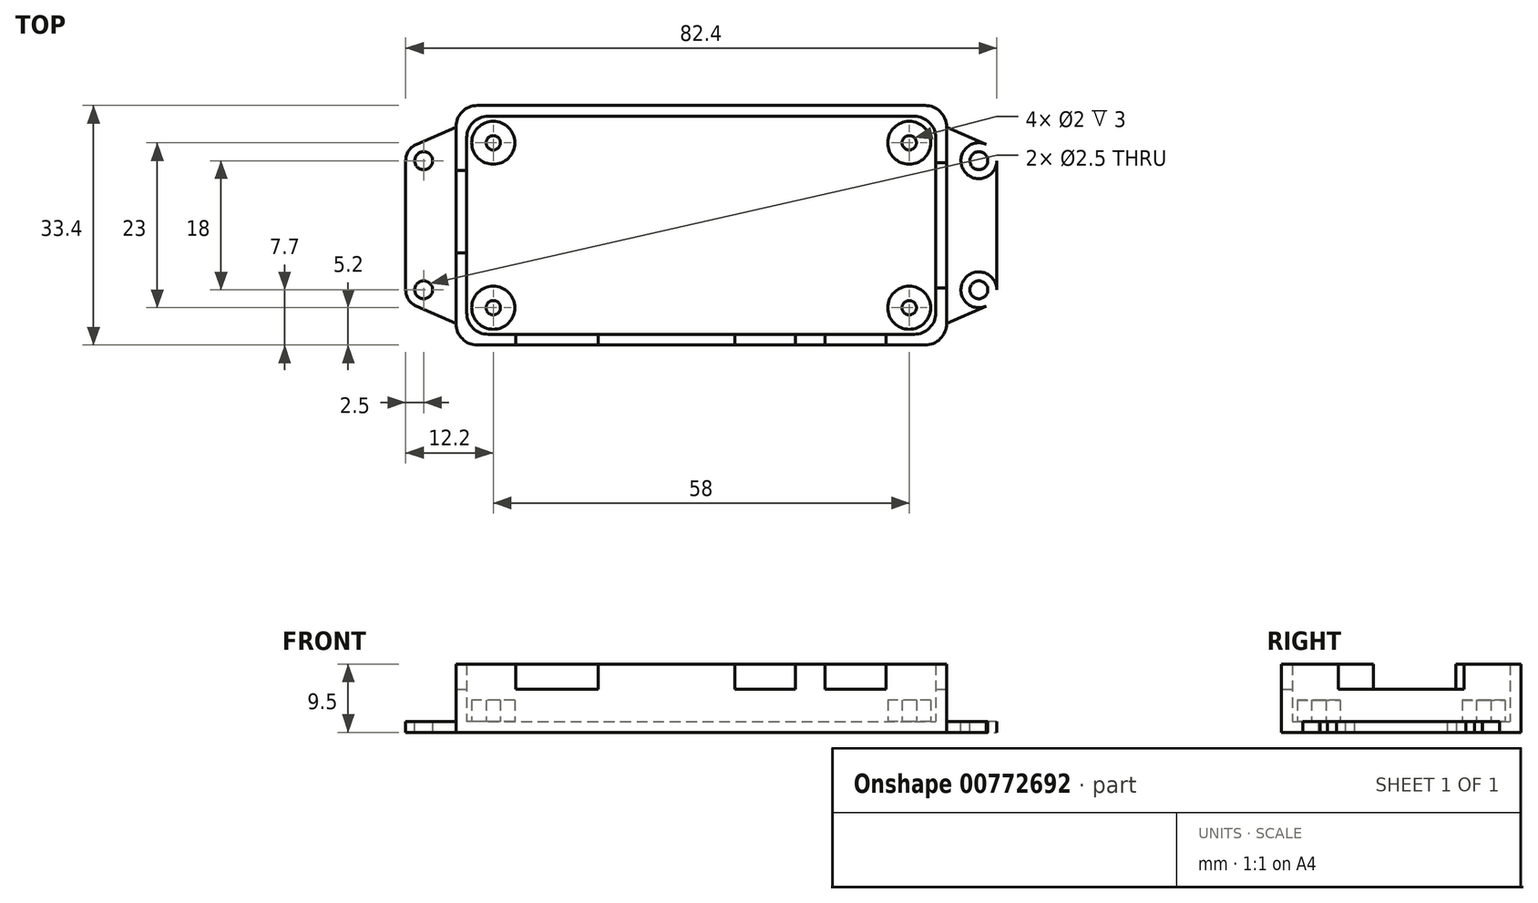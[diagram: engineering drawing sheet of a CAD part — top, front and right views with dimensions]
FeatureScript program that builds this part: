
annotation { "Feature Type Name" : "Feature", "Feature Type Description" : "" }
export const myFeature = defineFeature(function(context is Context, id is Id, definition is map)
    precondition{}
    {
        {
            var Q0;
            Q0=qCreatedBy(makeId("Top.planeOp"),FACE);
            var sketch = newSketch(context, id + "F0", { "sketchPlane" : qUnion([Q0])});
            skLineSegment(sketch, "E0", {"start": v(0, 31.79) * mm, "end": v(0, -34.92) * mm, "construction": true});
            skLineSegment(sketch, "E1", {"start": v(-57.68, 0) * mm, "end": v(57.82, 0) * mm, "construction": true});
            skLineSegment(sketch, "E2.bottom", {"start": v(-29.5, 15) * mm, "end": v(29.5, 15) * mm, "construction": true});
            skLineSegment(sketch, "E2.top", {"start": v(-29.5, -15) * mm, "end": v(29.5, -15) * mm, "construction": true});
            skLineSegment(sketch, "E2.left", {"start": v(-32.5, 12) * mm, "end": v(-32.5, -12) * mm, "construction": true});
            skLineSegment(sketch, "E2.right", {"start": v(32.5, 12) * mm, "end": v(32.5, -12) * mm, "construction": true});
            skPoint(sketch, "E3.visualSharp", {"position": v(-32.5, 15) * mm});
            skArc(sketch, "E3.filletArc", {"start": v(-29.5, 15) * mm, "mid": v(-31.62, 14.12) * mm, "end": v(-32.5, 12) * mm, "construction": true});
            skPoint(sketch, "E4.visualSharp", {"position": v(32.5, 15) * mm});
            skArc(sketch, "E4.filletArc", {"start": v(32.5, 12) * mm, "mid": v(31.62, 14.12) * mm, "end": v(29.5, 15) * mm, "construction": true});
            skPoint(sketch, "E5.visualSharp", {"position": v(32.5, -15) * mm});
            skArc(sketch, "E5.filletArc", {"start": v(29.5, -15) * mm, "mid": v(31.62, -14.12) * mm, "end": v(32.5, -12) * mm, "construction": true});
            skPoint(sketch, "E6.visualSharp", {"position": v(-32.5, -15) * mm});
            skArc(sketch, "E6.filletArc", {"start": v(-32.5, -12) * mm, "mid": v(-31.62, -14.12) * mm, "end": v(-29.5, -15) * mm, "construction": true});
            skCircle(sketch, "E7", {"center": v(-29, 11.5) * mm, "radius": 3 * mm});
            skCircle(sketch, "E8.0.1.0", {"center": v(-29, -11.5) * mm, "radius": 3 * mm});
            skCircle(sketch, "E8.1.0.0", {"center": v(29, 11.5) * mm, "radius": 3 * mm});
            skCircle(sketch, "E8.1.1.0", {"center": v(29, -11.5) * mm, "radius": 3 * mm});
            skLineSegment(sketch, "E8.direction1", {"start": v(-29, 11.5) * mm, "end": v(29, 11.5) * mm, "construction": true});
            skLineSegment(sketch, "E8.direction2", {"start": v(-29, 11.5) * mm, "end": v(-29, -11.5) * mm, "construction": true});
            skCircle(sketch, "E9", {"center": v(-29, 11.5) * mm, "radius": 1 * mm});
            skCircle(sketch, "E10.0.1.0", {"center": v(-29, -11.5) * mm, "radius": 1 * mm});
            skCircle(sketch, "E10.1.0.0", {"center": v(29, 11.5) * mm, "radius": 1 * mm});
            skCircle(sketch, "E10.1.1.0", {"center": v(29, -11.5) * mm, "radius": 1 * mm});
            skLineSegment(sketch, "E11.bottom", {"start": v(-29.7, 15.2) * mm, "end": v(29.7, 15.2) * mm});
            skLineSegment(sketch, "E11.top", {"start": v(-29.7, -15.2) * mm, "end": v(29.7, -15.2) * mm});
            skLineSegment(sketch, "E11.left", {"start": v(-32.7, 12.2) * mm, "end": v(-32.7, -12.2) * mm});
            skLineSegment(sketch, "E11.right", {"start": v(32.7, 12.2) * mm, "end": v(32.7, -12.2) * mm});
            skPoint(sketch, "E12.visualSharp", {"position": v(-32.7, 15.2) * mm});
            skArc(sketch, "E12.filletArc", {"start": v(-29.7, 15.2) * mm, "mid": v(-31.82, 14.32) * mm, "end": v(-32.7, 12.2) * mm});
            skPoint(sketch, "E13.visualSharp", {"position": v(-32.7, -15.2) * mm});
            skArc(sketch, "E13.filletArc", {"start": v(-32.7, -12.2) * mm, "mid": v(-31.82, -14.32) * mm, "end": v(-29.7, -15.2) * mm});
            skPoint(sketch, "E14.visualSharp", {"position": v(32.7, -15.2) * mm});
            skArc(sketch, "E14.filletArc", {"start": v(29.7, -15.2) * mm, "mid": v(31.82, -14.32) * mm, "end": v(32.7, -12.2) * mm});
            skPoint(sketch, "E15.visualSharp", {"position": v(32.7, 15.2) * mm});
            skArc(sketch, "E15.filletArc", {"start": v(32.7, 12.2) * mm, "mid": v(31.82, 14.32) * mm, "end": v(29.7, 15.2) * mm});
            skLineSegment(sketch, "E16.bottom", {"start": v(-31.2, 16.7) * mm, "end": v(31.2, 16.7) * mm});
            skLineSegment(sketch, "E16.top", {"start": v(-31.2, -16.7) * mm, "end": v(31.2, -16.7) * mm});
            skLineSegment(sketch, "E16.left", {"start": v(-34.2, 13.7) * mm, "end": v(-34.2, -13.7) * mm});
            skLineSegment(sketch, "E16.right", {"start": v(34.2, 13.7) * mm, "end": v(34.2, -13.7) * mm});
            skPoint(sketch, "E17.visualSharp", {"position": v(-34.2, 16.7) * mm});
            skArc(sketch, "E17.filletArc", {"start": v(-31.2, 16.7) * mm, "mid": v(-33.32, 15.82) * mm, "end": v(-34.2, 13.7) * mm});
            skPoint(sketch, "E18.visualSharp", {"position": v(-34.2, -16.7) * mm});
            skArc(sketch, "E18.filletArc", {"start": v(-34.2, -13.7) * mm, "mid": v(-33.32, -15.82) * mm, "end": v(-31.2, -16.7) * mm});
            skPoint(sketch, "E19.visualSharp", {"position": v(34.2, -16.7) * mm});
            skArc(sketch, "E19.filletArc", {"start": v(31.2, -16.7) * mm, "mid": v(33.32, -15.82) * mm, "end": v(34.2, -13.7) * mm});
            skPoint(sketch, "E20.visualSharp", {"position": v(34.2, 16.7) * mm});
            skArc(sketch, "E20.filletArc", {"start": v(34.2, 13.7) * mm, "mid": v(33.32, 15.82) * mm, "end": v(31.2, 16.7) * mm});
            skLineSegment(sketch, "E21", {"start": v(-36.24, 1.9) * mm, "end": v(-30.97, 1.9) * mm, "construction": true});
            skLineSegment(sketch, "E22", {"start": v(-20.1, -13.64) * mm, "end": v(-20.1, -19.07) * mm, "construction": true});
            skLineSegment(sketch, "E23", {"start": v(8.9, -12.93) * mm, "end": v(8.9, -18.66) * mm, "construction": true});
            skLineSegment(sketch, "E24", {"start": v(21.5, -12.58) * mm, "end": v(21.5, -18.71) * mm, "construction": true});
            skLineSegment(sketch, "E25", {"start": v(-25.85, -16.7) * mm, "end": v(-25.85, -15.2) * mm});
            skLineSegment(sketch, "E26", {"start": v(-14.35, -16.7) * mm, "end": v(-14.35, -15.2) * mm});
            skLineSegment(sketch, "E27", {"start": v(4.65, -16.7) * mm, "end": v(4.65, -15.2) * mm});
            skLineSegment(sketch, "E28", {"start": v(13.15, -15.2) * mm, "end": v(13.15, -16.7) * mm});
            skLineSegment(sketch, "E29", {"start": v(17.25, -16.7) * mm, "end": v(17.25, -15.2) * mm});
            skLineSegment(sketch, "E30", {"start": v(25.75, -15.2) * mm, "end": v(25.75, -16.7) * mm});
            skLineSegment(sketch, "E31", {"start": v(-34.2, 7.65) * mm, "end": v(-32.7, 7.65) * mm});
            skLineSegment(sketch, "E32", {"start": v(-34.2, -3.85) * mm, "end": v(-32.7, -3.85) * mm});
            skLineSegment(sketch, "E33", {"start": v(32.7, 8.75) * mm, "end": v(34.2, 8.75) * mm});
            skLineSegment(sketch, "E34", {"start": v(32.7, -8.75) * mm, "end": v(34.2, -8.75) * mm});
            skSolve(sketch);
        }
        {
            var Q0;
            Q0=qSketchRegion(id+"F0",true);
            var Q1;
            Q1=makeQuery(id+"F0.imprint","IMPRINT",FACE,{"disambiguationData":[TD([[makeQuery(id+"F0.imprint","IMPRINT",EDGE,{"derivedFrom":sQuery(id+"F0.wireOp",EDGE,"E7")}),-1.0]])]});
            var Q2;
            Q2=makeQuery(id+"F0.imprint","IMPRINT",FACE,{"disambiguationData":[TD([[makeQuery(id+"F0.imprint","IMPRINT",EDGE,{"derivedFrom":sQuery(id+"F0.wireOp",EDGE,"E10.0.1.0")}),1.0]])]});
            var Q3;
            Q3=makeQuery(id+"F0.imprint","IMPRINT",FACE,{"disambiguationData":[TD([[makeQuery(id+"F0.imprint","IMPRINT",EDGE,{"derivedFrom":sQuery(id+"F0.wireOp",EDGE,"E8.0.1.0")}),1.0]])]});
            var Q4;
            Q4=makeQuery(id+"F0.imprint","IMPRINT",FACE,{"disambiguationData":[TD([[makeQuery(id+"F0.imprint","IMPRINT",EDGE,{"derivedFrom":sQuery(id+"F0.wireOp",EDGE,"E9")}),1.0]])]});
            var Q5;
            Q5=makeQuery(id+"F0.imprint","IMPRINT",FACE,{"disambiguationData":[TD([[makeQuery(id+"F0.imprint","IMPRINT",EDGE,{"derivedFrom":sQuery(id+"F0.wireOp",EDGE,"E7")}),1.0]])]});
            var Q6;
            Q6=makeQuery(id+"F0.imprint","IMPRINT",FACE,{"disambiguationData":[TD([[makeQuery(id+"F0.imprint","IMPRINT",EDGE,{"derivedFrom":sQuery(id+"F0.wireOp",EDGE,"E10.1.1.0")}),1.0]])]});
            var Q7;
            Q7=makeQuery(id+"F0.imprint","IMPRINT",FACE,{"disambiguationData":[TD([[makeQuery(id+"F0.imprint","IMPRINT",EDGE,{"derivedFrom":sQuery(id+"F0.wireOp",EDGE,"E8.1.1.0")}),1.0]])]});
            var Q8;
            Q8=makeQuery(id+"F0.imprint","IMPRINT",FACE,{"disambiguationData":[TD([[makeQuery(id+"F0.imprint","IMPRINT",EDGE,{"derivedFrom":sQuery(id+"F0.wireOp",EDGE,"E10.1.0.0")}),1.0]])]});
            var Q9;
            Q9=makeQuery(id+"F0.imprint","IMPRINT",FACE,{"disambiguationData":[TD([[makeQuery(id+"F0.imprint","IMPRINT",EDGE,{"derivedFrom":sQuery(id+"F0.wireOp",EDGE,"E8.1.0.0")}),1.0]])]});
            extrude(context, id + "F1", {"entities" : qUnion([Q0, Q1, Q2, Q3, Q4, Q5, Q6, Q7, Q8, Q9]), "oppositeDirection" : true, "depth" : 1.5 * mm, "offsetDistance" : 25 * mm});
        }
        {
            var Q0;
            Q0=makeQuery(id+"F0.imprint","IMPRINT",FACE,{"disambiguationData":[TD([[makeQuery(id+"F0.imprint","IMPRINT",EDGE,{"derivedFrom":sQuery(id+"F0.wireOp",EDGE,"E7")}),1.0]])]});
            var Q1;
            Q1=makeQuery(id+"F0.imprint","IMPRINT",FACE,{"disambiguationData":[TD([[makeQuery(id+"F0.imprint","IMPRINT",EDGE,{"derivedFrom":sQuery(id+"F0.wireOp",EDGE,"E8.0.1.0")}),1.0]])]});
            var Q2;
            Q2=makeQuery(id+"F0.imprint","IMPRINT",FACE,{"disambiguationData":[TD([[makeQuery(id+"F0.imprint","IMPRINT",EDGE,{"derivedFrom":sQuery(id+"F0.wireOp",EDGE,"E8.1.0.0")}),1.0]])]});
            var Q3;
            Q3=makeQuery(id+"F0.imprint","IMPRINT",FACE,{"disambiguationData":[TD([[makeQuery(id+"F0.imprint","IMPRINT",EDGE,{"derivedFrom":sQuery(id+"F0.wireOp",EDGE,"E8.1.1.0")}),1.0]])]});
            extrude(context, id + "F2", {"entities" : qUnion([Q0, Q1, Q2, Q3]), "operationType" : NewBodyOperationType.ADD, "depth" : 3 * mm, "offsetDistance" : 25 * mm});
        }
        {
            var Q0;
            {var subQ3=sQuery(id+"F0.wireOp",EDGE,"E13.filletArc");Q0=makeQuery(id+"F0.imprint","IMPRINT",FACE,{"disambiguationData":[TD([[makeQuery(id+"F0.imprint","IMPRINT",EDGE,{"derivedFrom":subQ3}),-1.0]])]});}
            var Q1;
            Q1=makeQuery(id+"F0.imprint","IMPRINT",FACE,{"disambiguationData":[TD([[makeQuery(id+"F0.imprint","IMPRINT",EDGE,{"derivedFrom":sQuery(id+"F0.wireOp",EDGE,"E11.bottom")}),1.0]])]});
            var Q2;
            {var subQ0=sQuery(id+"F0.wireOp",EDGE,"E26");Q2=makeQuery(id+"F0.imprint","IMPRINT",FACE,{"disambiguationData":[TD([[makeQuery(id+"F0.imprint","IMPRINT",EDGE,{"derivedFrom":subQ0}),-1.0]])]});}
            var Q3;
            {var subQ0=sQuery(id+"F0.wireOp",EDGE,"E28");Q3=makeQuery(id+"F0.imprint","IMPRINT",FACE,{"disambiguationData":[TD([[makeQuery(id+"F0.imprint","IMPRINT",EDGE,{"derivedFrom":subQ0}),1.0]])]});}
            var Q4;
            {var subQ3=sQuery(id+"F0.wireOp",EDGE,"E14.filletArc");Q4=makeQuery(id+"F0.imprint","IMPRINT",FACE,{"disambiguationData":[TD([[makeQuery(id+"F0.imprint","IMPRINT",EDGE,{"derivedFrom":subQ3}),-1.0]])]});}
            extrude(context, id + "F3", {"entities" : qUnion([Q0, Q1, Q2, Q3, Q4]), "operationType" : NewBodyOperationType.ADD, "depth" : 8 * mm, "offsetDistance" : 25 * mm});
        }
        {
            var Q0;
            {var subQ0=sQuery(id+"F0.wireOp",EDGE,"E31");Q0=makeQuery(id+"F0.imprint","IMPRINT",FACE,{"disambiguationData":[TD([[makeQuery(id+"F0.imprint","IMPRINT",EDGE,{"derivedFrom":subQ0}),-1.0]])]});}
            var Q1;
            {var subQ0=sQuery(id+"F0.wireOp",EDGE,"E25");Q1=makeQuery(id+"F0.imprint","IMPRINT",FACE,{"disambiguationData":[TD([[makeQuery(id+"F0.imprint","IMPRINT",EDGE,{"derivedFrom":subQ0}),-1.0]])]});}
            var Q2;
            {var subQ0=sQuery(id+"F0.wireOp",EDGE,"E27");Q2=makeQuery(id+"F0.imprint","IMPRINT",FACE,{"disambiguationData":[TD([[makeQuery(id+"F0.imprint","IMPRINT",EDGE,{"derivedFrom":subQ0}),-1.0]])]});}
            var Q3;
            {var subQ0=sQuery(id+"F0.wireOp",EDGE,"E29");Q3=makeQuery(id+"F0.imprint","IMPRINT",FACE,{"disambiguationData":[TD([[makeQuery(id+"F0.imprint","IMPRINT",EDGE,{"derivedFrom":subQ0}),-1.0]])]});}
            var Q4;
            {var subQ0=sQuery(id+"F0.wireOp",EDGE,"E33");Q4=makeQuery(id+"F0.imprint","IMPRINT",FACE,{"disambiguationData":[TD([[makeQuery(id+"F0.imprint","IMPRINT",EDGE,{"derivedFrom":subQ0}),-1.0]])]});}
            extrude(context, id + "F4", {"entities" : qUnion([Q0, Q1, Q2, Q3, Q4]), "operationType" : NewBodyOperationType.ADD, "depth" : 4.5 * mm, "offsetDistance" : 25 * mm});
        }
        {
            var Q0;
            Q0=makeQuery(id+"F0.imprint","IMPRINT",FACE,{"disambiguationData":[TD([[makeQuery(id+"F0.imprint","IMPRINT",EDGE,{"derivedFrom":sQuery(id+"F0.wireOp",EDGE,"E7")}),-1.0]])]});
            var sketch = newSketch(context, id + "F5", { "sketchPlane" : qUnion([Q0])});
            skLineSegment(sketch, "E35.0", {"start": v(-34.2, 13.7) * mm, "end": v(-34.2, -13.7) * mm});
            skLineSegment(sketch, "E36.0", {"start": v(34.2, 13.7) * mm, "end": v(34.2, -13.7) * mm});
            skLineSegment(sketch, "E37", {"start": v(-34.2, 13.7) * mm, "end": v(-39.7, 11.3) * mm});
            skLineSegment(sketch, "E38", {"start": v(-41.2, 9) * mm, "end": v(-41.2, -9) * mm});
            skLineSegment(sketch, "E39", {"start": v(-39.7, -11.3) * mm, "end": v(-34.2, -13.7) * mm});
            skCircle(sketch, "E40", {"center": v(-38.7, -9) * mm, "radius": 2.5 * mm});
            skCircle(sketch, "E41", {"center": v(-38.7, 9) * mm, "radius": 2.5 * mm});
            skCircle(sketch, "E42", {"center": v(-38.7, 9) * mm, "radius": 1.25 * mm});
            skCircle(sketch, "E43", {"center": v(-38.7, -9) * mm, "radius": 1.25 * mm});
            skLineSegment(sketch, "E44.MirrorCS", {"start": v(39.7, -11.3) * mm, "end": v(34.2, -13.7) * mm});
            skCircle(sketch, "E45.MirrorC", {"center": v(38.7, -9) * mm, "radius": 1.25 * mm});
            skCircle(sketch, "E46.MirrorC", {"center": v(38.7, -9) * mm, "radius": 2.5 * mm});
            skCircle(sketch, "E47.MirrorC", {"center": v(38.7, 9) * mm, "radius": 1.25 * mm});
            skCircle(sketch, "E48.MirrorC", {"center": v(38.7, 9) * mm, "radius": 2.5 * mm});
            skLineSegment(sketch, "E49.MirrorCS", {"start": v(41.2, 9) * mm, "end": v(41.2, -9) * mm});
            skLineSegment(sketch, "E50.MirrorCS", {"start": v(34.2, 13.7) * mm, "end": v(39.7, 11.3) * mm});
            skSolve(sketch);
        }
        {
            var Q0;
            {var subQ4=sQuery(id+"F5.wireOp",EDGE,"E44.MirrorCS");Q0=makeQuery(id+"F5.imprint","IMPRINT",FACE,{"disambiguationData":[TD([[makeQuery(id+"F5.imprint","IMPRINT",EDGE,{"derivedFrom":subQ4}),-1.0]])]});}
            var Q1;
            Q1=makeQuery(id+"F5.imprint","IMPRINT",FACE,{"disambiguationData":[TD([[makeQuery(id+"F5.imprint","IMPRINT",EDGE,{"derivedFrom":sQuery(id+"F5.wireOp",EDGE,"E45.MirrorC")}),1.0]])]});
            var Q2;
            Q2=makeQuery(id+"F5.imprint","IMPRINT",FACE,{"disambiguationData":[TD([[makeQuery(id+"F5.imprint","IMPRINT",EDGE,{"derivedFrom":sQuery(id+"F5.wireOp",EDGE,"E47.MirrorC")}),1.0]])]});
            var Q3;
            Q3=makeQuery(id+"F5.imprint","IMPRINT",FACE,{"disambiguationData":[TD([[makeQuery(id+"F5.imprint","IMPRINT",EDGE,{"derivedFrom":sQuery(id+"F5.wireOp",EDGE,"E35.0")}),-1.0]])]});
            var Q4;
            Q4=makeQuery(id+"F5.imprint","IMPRINT",FACE,{"disambiguationData":[TD([[makeQuery(id+"F5.imprint","IMPRINT",EDGE,{"derivedFrom":sQuery(id+"F5.wireOp",EDGE,"E42")}),-1.0]])]});
            var Q5;
            Q5=makeQuery(id+"F5.imprint","IMPRINT",FACE,{"disambiguationData":[TD([[makeQuery(id+"F5.imprint","IMPRINT",EDGE,{"derivedFrom":sQuery(id+"F5.wireOp",EDGE,"E43")}),-1.0]])]});
            extrude(context, id + "F6", {"entities" : qUnion([Q0, Q1, Q2, Q3, Q4, Q5]), "operationType" : NewBodyOperationType.ADD, "oppositeDirection" : true, "depth" : 1.5 * mm, "offsetDistance" : 25 * mm});
        }
    });
